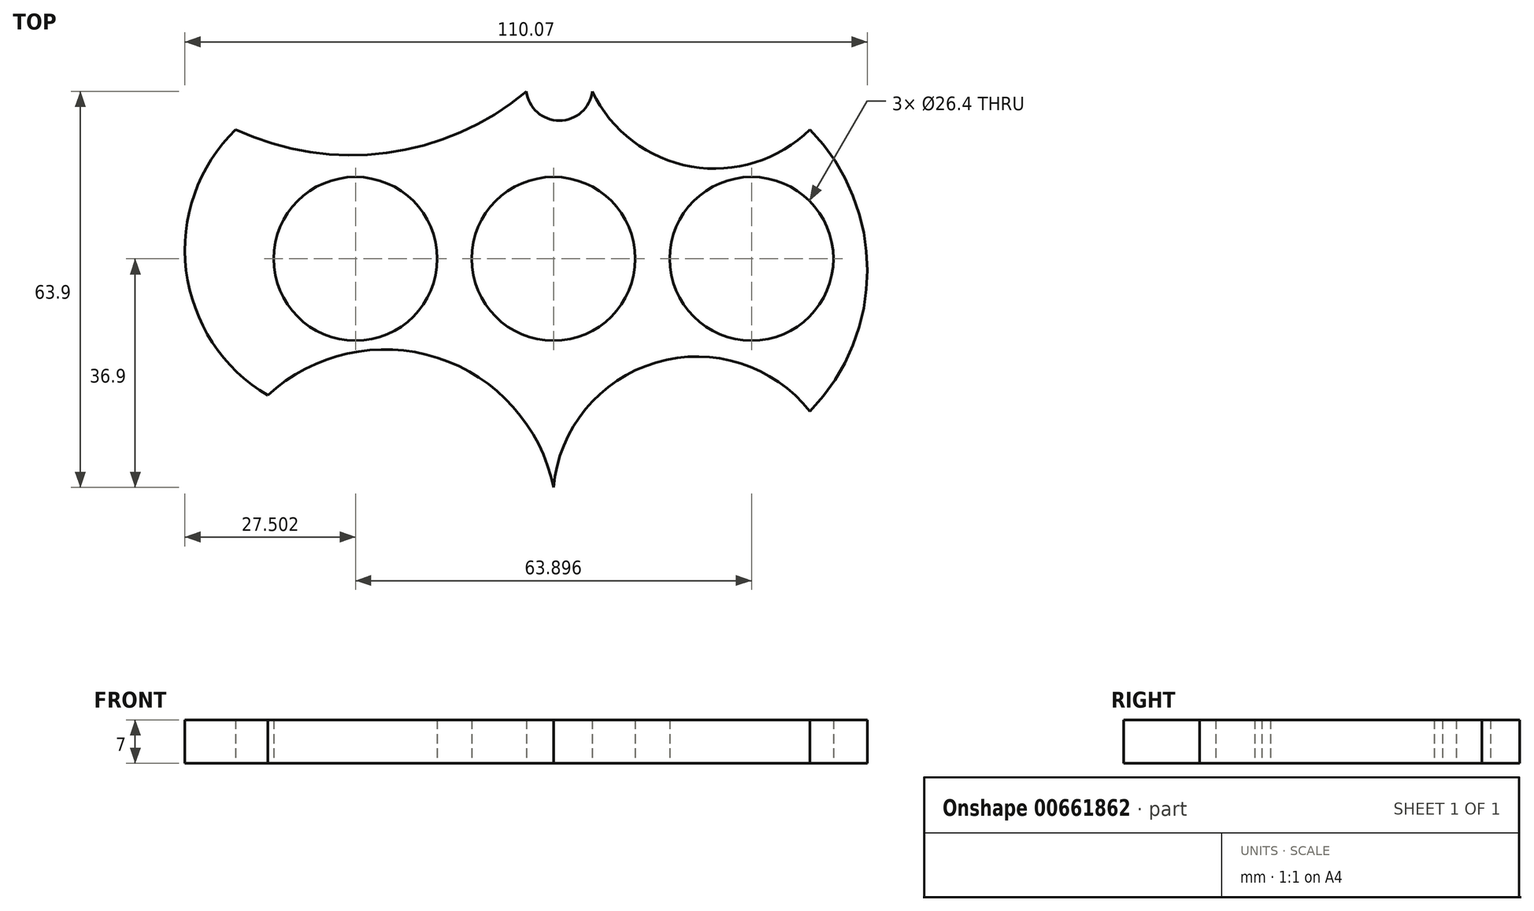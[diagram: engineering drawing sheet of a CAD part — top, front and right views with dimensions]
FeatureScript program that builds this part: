
annotation { "Feature Type Name" : "Feature", "Feature Type Description" : "" }
export const myFeature = defineFeature(function(context is Context, id is Id, definition is map)
    precondition{}
    {
        {
            var Q0;
            Q0=qCreatedBy(makeId("Top.planeOp"),FACE);
            var sketch = newSketch(context, id + "F0", { "sketchPlane" : qUnion([Q0])});
            skCircle(sketch, "E0", {"center": v(31.95, 0) * mm, "radius": 11.2 * mm});
            skCircle(sketch, "E1", {"center": v(31.95, 0) * mm, "radius": 13.2 * mm});
            skCircle(sketch, "E2", {"center": v(-31.95, 0) * mm, "radius": 11.2 * mm});
            skCircle(sketch, "E3", {"center": v(-31.95, 0) * mm, "radius": 13.2 * mm});
            skArc(sketch, "E4", {"start": v(41.38, -24.64) * mm, "mid": v(50.62, -1.89) * mm, "end": v(41.38, 20.87) * mm});
            skArc(sketch, "E5", {"start": v(6.25, 27) * mm, "mid": v(22.23, 14.88) * mm, "end": v(41.38, 20.87) * mm});
            skArc(sketch, "E6", {"start": v(-4.36, 27) * mm, "mid": v(0.94, 22.3) * mm, "end": v(6.25, 27) * mm});
            skArc(sketch, "E7", {"start": v(-51.28, 20.87) * mm, "mid": v(-26.93, 17.09) * mm, "end": v(-4.36, 27) * mm});
            skArc(sketch, "E8", {"start": v(-51.28, 20.87) * mm, "mid": v(-59.25, -1.87) * mm, "end": v(-46.1, -22.05) * mm});
            skArc(sketch, "E9", {"start": v(0, -36.9) * mm, "mid": v(-18.7, -15.98) * mm, "end": v(-46.1, -22.05) * mm});
            skArc(sketch, "E10", {"start": v(41.38, -24.64) * mm, "mid": v(16.53, -16.73) * mm, "end": v(0, -36.9) * mm});
            skCircle(sketch, "E11", {"center": v(0, 0) * mm, "radius": 11.2 * mm});
            skCircle(sketch, "E12", {"center": v(0, 0) * mm, "radius": 13.2 * mm});
            skSolve(sketch);
        }
        {
            var Q0;
            Q0=makeQuery(id+"F0.imprint","IMPRINT",FACE,{"disambiguationData":[TD([[makeQuery(id+"F0.imprint","IMPRINT",EDGE,{"derivedFrom":sQuery(id+"F0.wireOp",EDGE,"E1")}),-1.0]])]});
            extrude(context, id + "F1", {"entities" : qUnion([Q0]), "depth" : 7 * mm, "offsetDistance" : 25 * mm});
        }
    });
